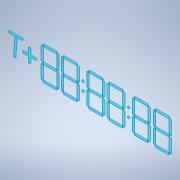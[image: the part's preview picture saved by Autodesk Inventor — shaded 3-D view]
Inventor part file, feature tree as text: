
AUTODESK INVENTOR PART (.ipt)
format: ipt  version: 2021 (Build 250183000, 183)  size: 862,208 bytes
history: native  units: mm
features: other x28, extrude x1, sketch x1
ambient origin geometry x8: Origin, YZ Plane, XZ Plane, XY Plane, X Axis, Y Axis, Z Axis, Center Point
bodies: Solid1 (feature_tree)
feature tree (30):
  other  "Blocks"
  extrude  "Extrusion1"  Depth=2.0mm TaperAngle=0.0deg
  sketch  "Sketch2"  dims[d0=3.2mm d1=3.2mm d2=3.2mm d3=3.2mm d4=3.2mm d5=3.2mm d6=3.2mm d7=3.2mm d8=2.0mm d9=2.0mm d10=2.0mm d11=2.0mm d12=3.2mm d13=3.2mm d14=8.0mm d15=3.2mm d16=3.2mm d17=57.0mm d18=3.2mm d19=3.2mm d20=3.2mm d21=3.2mm d22=3.2mm d23=3.2mm d24=3.2mm d25=3.2mm d26=3.2mm d27=3.2mm d28=3.2mm d29=1.0mm d30=8.0mm d31=8.0mm d32=3.2mm d33=3.2mm d34=50.0mm d35=135.0deg d36=50.0mm d37=135.0deg d38=4.0mm d39=4.0mm d40=1.1mm d41=1.1mm d42=1.1mm d43=1.1mm d44=1.1mm d45=1.1mm d46=1.1mm d47=1.1mm d48=1.1mm d49=1.1mm d50=1.1mm d51=1.1mm d52=1.1mm d53=1.1mm d54=1.1mm d55=1.1mm d56=3.2mm d57=3.2mm d58=3.2mm d59=3.2mm d60=3.2mm d61=3.2mm d62=3.2mm d63=3.2mm d64=3.2mm d65=3.2mm d66=3.2mm d67=3.2mm d68=3.2mm d69=0.0mm d70=0.0mm d71=8.0mm d72=8.0mm d73=0.0mm d74=0.0mm d75=3.2mm d76=3.2mm d77=3.2mm d78=90.0deg d79=17.6mm d80=17.6mm d81=17.6mm d82=17.6mm d83=17.6mm d84=0.0mm d85=17.6mm d86=1.0mm d87=1.0mm d88=0.0mm d89=0.0mm d90=0.0mm d91=0.0mm d92=10.0mm d93=7.5mm d94=25.0mm d95=7.5mm d96=25.0mm d97=1.1mm d98=21.0mm d99=21.0mm d100=21.0mm d101=0.0mm d102=21.0mm d103=21.0mm d104=0.0mm d105=21.0mm d106=39.0mm d107=0.0mm d108=18.0mm d109=23.0mm d110=11.5mm d111=11.5mm d112=11.5mm d113=0.0mm d114=11.5mm d115=0.0mm d116=0.0mm d117=0.0mm d118=0.0mm d119=10.0mm d120=7.5mm d121=25.0mm d122=7.5mm d123=25.0mm d124=1.1mm d125=21.0mm d126=21.0mm d127=21.0mm d128=0.0mm d129=21.0mm d130=21.0mm d131=0.0mm d132=21.0mm d133=39.0mm d134=0.0mm d135=18.0mm d136=23.0mm d137=11.5mm d138=11.5mm d139=11.5mm d140=0.0mm d141=11.5mm d142=2.0mm d143=0.0mm d144=0.5mm d145=0.872665mm]
  other  "Dot"
  other  "Slanted Segment Large"
  other  "Single Segment"
  other  "7 Segment Digit"
  other  "+ sign"
  other  "Clock Face with T +-"
  other  "Single Segment:1"
  other  "Single Segment:2"
  other  "Single Segment:3"
  other  "Single Segment:4"
  other  "Single Segment:5"
  other  "Single Segment:6"
  other  "Single Segment:7"
  other  "Dot:5"
  other  "Dot:6"
  other  "Dot:7"
  other  "Dot:8"
  other  "Slanted Segment Large:2"
  other  "7 Segment Digit:7"
  other  "Single Segment:9"
  other  "7 Segment Digit:8"
  other  "7 Segment Digit:9"
  other  "7 Segment Digit:10"
  other  "7 Segment Digit:11"
  other  "7 Segment Digit:12"
  other  "+ sign:2"
  other  "Clock Face with T +-:1"
